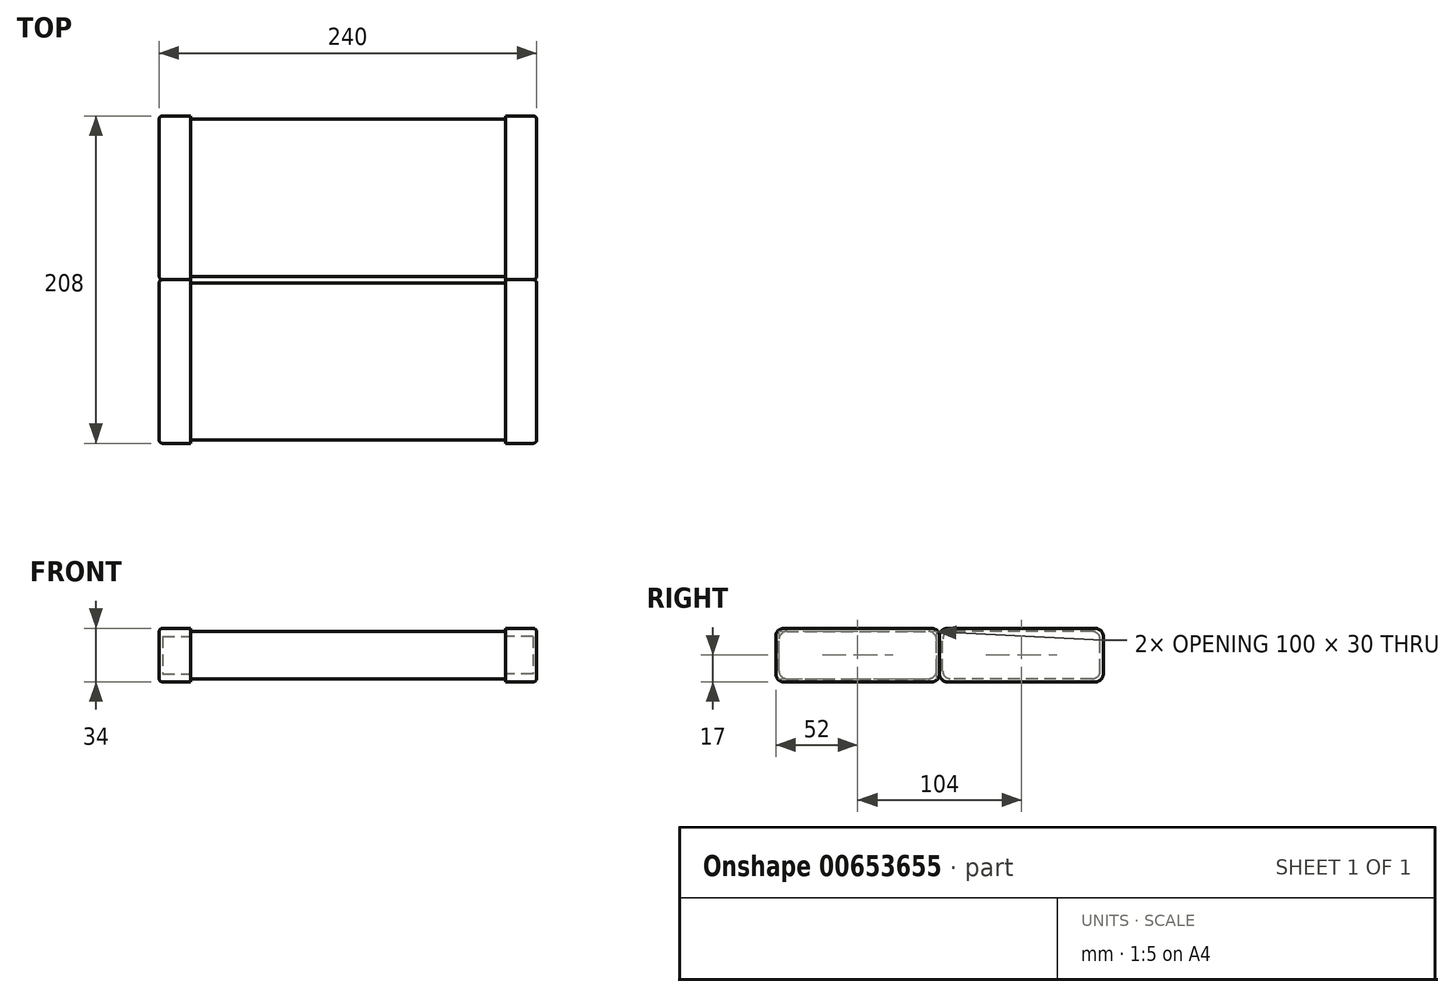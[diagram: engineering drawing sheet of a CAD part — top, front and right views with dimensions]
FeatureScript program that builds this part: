
annotation { "Feature Type Name" : "Feature", "Feature Type Description" : "" }
export const myFeature = defineFeature(function(context is Context, id is Id, definition is map)
    precondition{}
    {
        {
            var Q0;
            Q0=qCreatedBy(makeId("Right.planeOp"),FACE);
            var sketch = newSketch(context, id + "F0", { "sketchPlane" : qUnion([Q0])});
            skLineSegment(sketch, "E0.bottom", {"start": v(0, 0) * mm, "end": v(100, 0) * mm});
            skLineSegment(sketch, "E0.top", {"start": v(0, 30) * mm, "end": v(100, 30) * mm});
            skLineSegment(sketch, "E0.left", {"start": v(0, 0) * mm, "end": v(0, 30) * mm});
            skLineSegment(sketch, "E0.right", {"start": v(100, 0) * mm, "end": v(100, 30) * mm});
            skSolve(sketch);
        }
        {
            var Q0;
            Q0 = qSketchRegion(id + "F0", true);
            extrude(context, id + "F1", {"entities" : qUnion([Q0]), "depth" : 100 * mm, "offsetDistance" : 25 * mm});
        }
        {
            var Q0;
            Q0=makeQuery(id+"F1.opExtrude","CAP_FACE",FACE,{"disambiguationData":[OSD([sQuery(id+"F0.wireOp",EDGE,"E0.bottom"),sQuery(id+"F0.wireOp",EDGE,"E0.top"),sQuery(id+"F0.wireOp",EDGE,"E0.left"),sQuery(id+"F0.wireOp",EDGE,"E0.right")])],"isStart":true});
            var sketch = newSketch(context, id + "F2", { "sketchPlane" : qUnion([Q0])});
            skLineSegment(sketch, "E1.bottom", {"start": v(-102, 32) * mm, "end": v(2, 32) * mm});
            skLineSegment(sketch, "E1.top", {"start": v(-102, -2) * mm, "end": v(2, -2) * mm});
            skLineSegment(sketch, "E1.left", {"start": v(-102, 32) * mm, "end": v(-102, -2) * mm});
            skLineSegment(sketch, "E1.right", {"start": v(2, 32) * mm, "end": v(2, -2) * mm});
            skSolve(sketch);
        }
        {
            var Q0;
            Q0=makeQuery(id+"F2.imprint","IMPRINT",FACE,{"disambiguationData":[TD([[makeQuery(id+"F2.imprint","IMPRINT",EDGE,{"derivedFrom":sQuery(id+"F2.wireOp",EDGE,"E1.bottom")}),-1.0]])]});
            var Q1;
            Q1=makeQuery(id+"F2.imprint","IMPRINT",FACE,{"disambiguationData":[TD([[makeQuery(id+"F2.imprint","IMPRINT",EDGE,{"derivedFrom":makeQuery(id+"F1.opExtrude","CAP_EDGE",EDGE,{"disambiguationData":[OSD([sQuery(id+"F0.wireOp",EDGE,"E0.bottom")])],"isStart":true})}),-1.0]])]});
            extrude(context, id + "F3", {"entities" : qUnion([Q0, Q1]), "operationType" : NewBodyOperationType.ADD, "depth" : 20 * mm, "offsetDistance" : 25 * mm});
        }
        {
            var Q0;
            Q0=makeQuery(id+"F1.opExtrude","SWEPT_EDGE",EDGE,{"disambiguationData":[OSD([sQuery(id+"F0.wireOp",EDGE,"E0.top"),sQuery(id+"F0.wireOp",EDGE,"E0.left")])]});
            var Q1;
            Q1=makeQuery(id+"F1.opExtrude","SWEPT_EDGE",EDGE,{"disambiguationData":[OSD([sQuery(id+"F0.wireOp",EDGE,"E0.bottom"),sQuery(id+"F0.wireOp",EDGE,"E0.left")])]});
            var Q2;
            Q2=makeQuery(id+"F1.opExtrude","SWEPT_EDGE",EDGE,{"disambiguationData":[OSD([sQuery(id+"F0.wireOp",EDGE,"E0.top"),sQuery(id+"F0.wireOp",EDGE,"E0.right")])]});
            var Q3;
            Q3=makeQuery(id+"F1.opExtrude","SWEPT_EDGE",EDGE,{"disambiguationData":[OSD([sQuery(id+"F0.wireOp",EDGE,"E0.bottom"),sQuery(id+"F0.wireOp",EDGE,"E0.right")])]});
            var Q4;
            Q4=makeQuery(id+"F3.opExtrude","SWEPT_EDGE",EDGE,{"disambiguationData":[OSD([sQuery(id+"F2.wireOp",EDGE,"E1.bottom"),sQuery(id+"F2.wireOp",EDGE,"E1.left")])]});
            var Q5;
            Q5=makeQuery(id+"F3.opExtrude","SWEPT_EDGE",EDGE,{"disambiguationData":[OSD([sQuery(id+"F2.wireOp",EDGE,"E1.top"),sQuery(id+"F2.wireOp",EDGE,"E1.left")])]});
            var Q6;
            Q6=makeQuery(id+"F3.opExtrude","SWEPT_EDGE",EDGE,{"disambiguationData":[OSD([sQuery(id+"F2.wireOp",EDGE,"E1.bottom"),sQuery(id+"F2.wireOp",EDGE,"E1.right")])]});
            var Q7;
            Q7=makeQuery(id+"F3.opExtrude","SWEPT_EDGE",EDGE,{"disambiguationData":[OSD([sQuery(id+"F2.wireOp",EDGE,"E1.top"),sQuery(id+"F2.wireOp",EDGE,"E1.right")])]});
            fillet(context, id + "F4", {"entities" : qUnion([Q0, Q1, Q2, Q3, Q4, Q5, Q6, Q7]), "radius" : 5 * mm, "tangentPropagation" : true, "allowEdgeOverflow" : false});
        }
        {
            var Q0;
            Q0=makeQuery(id+"F1.opExtrude","SWEPT_BODY",BODY,{"disambiguationData":[OSD([sQuery(id+"F0.wireOp",EDGE,"E0.bottom"),sQuery(id+"F0.wireOp",EDGE,"E0.top"),sQuery(id+"F0.wireOp",EDGE,"E0.left"),sQuery(id+"F0.wireOp",EDGE,"E0.right")])]});
            var Q1;
            Q1=makeQuery(id+"F1.opExtrude","CAP_FACE",FACE,{"disambiguationData":[OSD([sQuery(id+"F0.wireOp",EDGE,"E0.bottom"),sQuery(id+"F0.wireOp",EDGE,"E0.top"),sQuery(id+"F0.wireOp",EDGE,"E0.left"),sQuery(id+"F0.wireOp",EDGE,"E0.right")])],"isStart":false});
            mirror(context, id + "F5", {"operationType" : NewBodyOperationType.ADD, "entities" : qUnion([Q0]), "mirrorPlane" : qUnion([Q1])});
        }
        {
            var Q0;
            Q0=makeQuery(id+"F3.opExtrude","CAP_FACE",FACE,{"disambiguationData":[OSD([sQuery(id+"F2.wireOp",EDGE,"E1.bottom"),sQuery(id+"F2.wireOp",EDGE,"E1.top"),sQuery(id+"F2.wireOp",EDGE,"E1.left"),sQuery(id+"F2.wireOp",EDGE,"E1.right")])],"isStart":false});
            var Q1;
            Q1=makeQuery(id+"F5.opPattern","COPY",FACE,{"derivedFrom":makeQuery(id+"F3.opExtrude","CAP_FACE",FACE,{"disambiguationData":[OSD([sQuery(id+"F2.wireOp",EDGE,"E1.bottom"),sQuery(id+"F2.wireOp",EDGE,"E1.top"),sQuery(id+"F2.wireOp",EDGE,"E1.left"),sQuery(id+"F2.wireOp",EDGE,"E1.right")])],"isStart":false}),"instanceName":"1"});
            fillet(context, id + "F6", {"entities" : qUnion([Q0, Q1]), "radius" : 2.5 * mm, "tangentPropagation" : true, "allowEdgeOverflow" : false});
        }
        {
            var Q0;
            Q0=makeQuery(id+"F1.opExtrude","SWEPT_BODY",BODY,{"disambiguationData":[OSD([sQuery(id+"F0.wireOp",EDGE,"E0.bottom"),sQuery(id+"F0.wireOp",EDGE,"E0.top"),sQuery(id+"F0.wireOp",EDGE,"E0.left"),sQuery(id+"F0.wireOp",EDGE,"E0.right")])]});
            var Q1;
            Q1=makeQuery(id+"F3.opExtrude","SWEPT_FACE",FACE,{"disambiguationData":[OSD([sQuery(id+"F2.wireOp",EDGE,"E1.left")])]});
            mirror(context, id + "F7", {"operationType" : NewBodyOperationType.ADD, "entities" : qUnion([Q0]), "mirrorPlane" : qUnion([Q1])});
        }
    });
